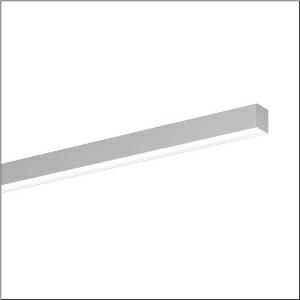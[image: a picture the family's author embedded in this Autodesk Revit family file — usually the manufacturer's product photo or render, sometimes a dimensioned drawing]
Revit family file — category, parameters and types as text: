
# Revit family: silica_r__21_51mx20dc45sb_4e07
name_source: partatom
category: Lighting Fixtures
units: mm (PartAtom-declared; Revit-internal decimal feet)

## family parameters
Cut with Voids When Loaded = No
Host = Face
Light Source = No
Part Type = Normal
Room Calculation Point = No
Round Connector Dimension = Use Diameter
Shared = No

## types (1)
- --- (1 x LED, 6000 lm, 40.1 W, 4000K)
    Apparent Load = 40 VA
    CIE Flux Codes = 48 79 96 100 100
    Color Rendering = 80
    Color Temperature = 4000K
    Default Elevation = 1800 mm
    Description = Silica® 21, office luminaire, primary optical cover: cover, of PMMA, opal, light emission: direct distribution, primary light characteristic: symmetric, installation type: surface-mounted, LED, rated luminous flux: 6.000lm, luminous efficacy: 150lm/W, light colour: 840, colour temperature: 4000K, control gear: DALI 2, with terminal, 3+2-pole, max. 2.5mm², mains connection: 220..240V, AC, 50/60Hz, rated input power: 40.1W, luminaire housing, of aluminium, metallic grey (RAL 9006), length: 3.004mm, width: 53mm, height: 53mm, protection rating (complete): IP20, insulation class (complete): insulation class I (protective earthing), certification: CE, permissible operating ambient temperature: 0..+35°C, standard: EN 50419, packaging unit: 1 piece
    Height = 53 mm
    Lamp = 1 x LED
    Lamp Light Flux = 6000 lm
    Lamp Power = 40.1 W
    Lamp count = 1
    Length = 3004 mm
    Luminous efficacy = 150 lm/W
    Manufacturer = Siteco
    ModVariant = No
    Model = 51MX20DC45SB
    Mounting Place = Ceiling
    Mounting Type = Surface mounted
    Number of Poles = 1
    OnlyDefault = Yes
    Power Factor = 1
    Product Name = Silica® 21
    Product group = office luminaire | ceiling mounted
    ProductGroupID = 302
    Protection Class = Protection class I
    Protection Degree = IP 20
    RLX_Detail_Level = 1
    RLX_Emergency_Light_Flux = 0 lm
    RLX_Emergency_Type = 0
    RLX_Emergency_Type_DB = No
    RlxData = <blob elided: 26297 chars, md5=0732355f>
    Socket = socket
    Standby Power = 0 W
    System Light Flux = 6000 lm
    System Power = 40 W
    Type Comments = factory setting: luminous flux: 100 % | dim-lin: 254 | 218 mA
    Type Image = l_1335933.jpg
    URL = http://relux.com
    VarID = @adj_117760
    Voltage = 0 V
    Weight = 0.00 kg
    Width = 53 mm

## geometry (parser evidence)
native form markers: Blend x4, Sweep x12
no freeform markers — native parametric forms only
